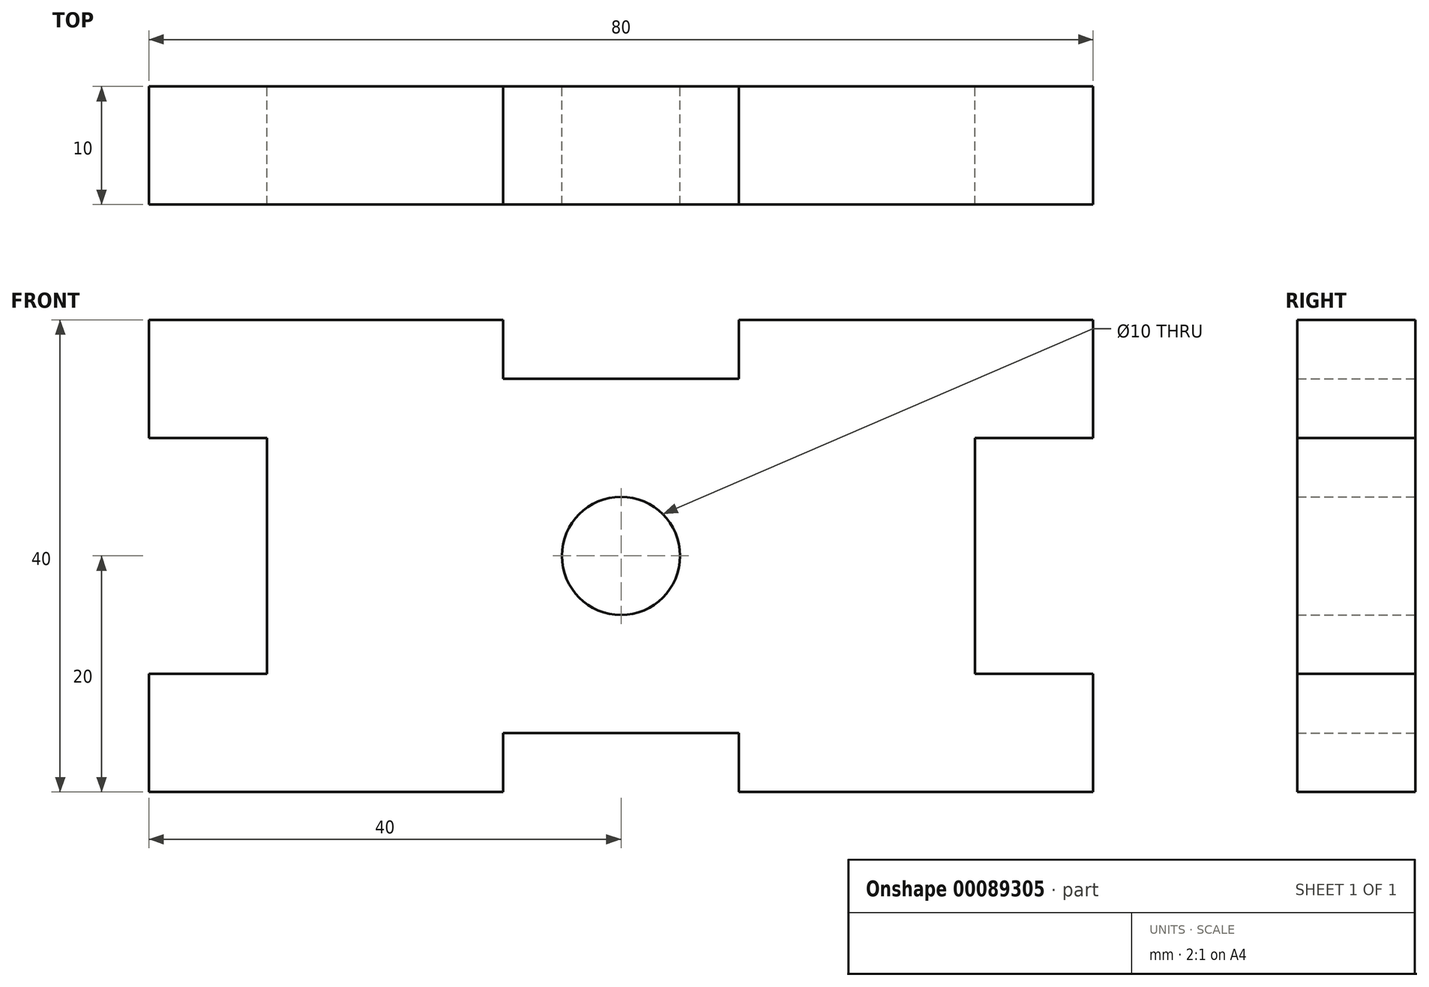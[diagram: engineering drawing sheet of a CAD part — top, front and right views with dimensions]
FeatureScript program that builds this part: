
annotation { "Feature Type Name" : "Feature", "Feature Type Description" : "" }
export const myFeature = defineFeature(function(context is Context, id is Id, definition is map)
    precondition{}
    {
        {
            var Q0;
            Q0=qCreatedBy(makeId("Front.planeOp"),FACE);
            var sketch = newSketch(context, id + "F0", { "sketchPlane" : qUnion([Q0])});
            skArc(sketch, "E0", {"start": v(5, 0) * mm, "mid": v(3.54, 3.54) * mm, "end": v(0, 5) * mm});
            skLineSegment(sketch, "E1", {"start": v(5, 0) * mm, "end": v(30, 0) * mm, "construction": true});
            skLineSegment(sketch, "E2", {"start": v(30, 0) * mm, "end": v(30, 10) * mm});
            skLineSegment(sketch, "E3", {"start": v(30, 10) * mm, "end": v(40, 10) * mm});
            skLineSegment(sketch, "E4", {"start": v(40, 10) * mm, "end": v(40, 20) * mm});
            skLineSegment(sketch, "E5", {"start": v(40, 20) * mm, "end": v(10, 20) * mm});
            skLineSegment(sketch, "E6", {"start": v(10, 20) * mm, "end": v(10, 15) * mm});
            skLineSegment(sketch, "E7", {"start": v(0, 5) * mm, "end": v(0, 15) * mm, "construction": true});
            skLineSegment(sketch, "E8", {"start": v(0, 15) * mm, "end": v(10, 15) * mm});
            skArc(sketch, "E9.MirrorCS", {"start": v(-5, 0) * mm, "mid": v(-3.54, 3.54) * mm, "end": v(0, 5) * mm});
            skLineSegment(sketch, "E10.MirrorCS", {"start": v(-40, 20) * mm, "end": v(-10, 20) * mm});
            skLineSegment(sketch, "E11.MirrorCS", {"start": v(-5, 0) * mm, "end": v(-30, 0) * mm, "construction": true});
            skLineSegment(sketch, "E12.MirrorCS", {"start": v(-30, 10) * mm, "end": v(-40, 10) * mm});
            skLineSegment(sketch, "E13.MirrorCS", {"start": v(-10, 20) * mm, "end": v(-10, 15) * mm});
            skLineSegment(sketch, "E14.MirrorCS", {"start": v(-40, 10) * mm, "end": v(-40, 20) * mm});
            skLineSegment(sketch, "E15.MirrorCS", {"start": v(0, 15) * mm, "end": v(-10, 15) * mm});
            skLineSegment(sketch, "E16.MirrorCS", {"start": v(-30, 0) * mm, "end": v(-30, 10) * mm});
            skLineSegment(sketch, "E17.MirrorCS", {"start": v(0, -15) * mm, "end": v(-10, -15) * mm});
            skArc(sketch, "E18.MirrorCS", {"start": v(5, 0) * mm, "mid": v(3.54, -3.54) * mm, "end": v(0, -5) * mm});
            skLineSegment(sketch, "E19.MirrorCS", {"start": v(-40, -10) * mm, "end": v(-40, -20) * mm});
            skLineSegment(sketch, "E20.MirrorCS", {"start": v(30, 0) * mm, "end": v(30, -10) * mm});
            skLineSegment(sketch, "E21.MirrorCS", {"start": v(30, -10) * mm, "end": v(40, -10) * mm});
            skLineSegment(sketch, "E22.MirrorCS", {"start": v(40, -10) * mm, "end": v(40, -20) * mm});
            skLineSegment(sketch, "E23.MirrorCS", {"start": v(40, -20) * mm, "end": v(10, -20) * mm});
            skLineSegment(sketch, "E24.MirrorCS", {"start": v(10, -20) * mm, "end": v(10, -15) * mm});
            skLineSegment(sketch, "E25.MirrorCS", {"start": v(0, -5) * mm, "end": v(0, -15) * mm, "construction": true});
            skLineSegment(sketch, "E26.MirrorCS", {"start": v(0, -15) * mm, "end": v(10, -15) * mm});
            skArc(sketch, "E27.MirrorCS", {"start": v(-5, 0) * mm, "mid": v(-3.54, -3.54) * mm, "end": v(0, -5) * mm});
            skLineSegment(sketch, "E28.MirrorCS", {"start": v(-30, -10) * mm, "end": v(-40, -10) * mm});
            skLineSegment(sketch, "E29.MirrorCS", {"start": v(-40, -20) * mm, "end": v(-10, -20) * mm});
            skLineSegment(sketch, "E30.MirrorCS", {"start": v(-10, -20) * mm, "end": v(-10, -15) * mm});
            skLineSegment(sketch, "E31.MirrorCS", {"start": v(-30, 0) * mm, "end": v(-30, -10) * mm});
            skSolve(sketch);
        }
        {
            var Q0;
            Q0=makeQuery(id+"F0.imprint","IMPRINT",FACE,{"disambiguationData":[TD([[makeQuery(id+"F0.imprint","IMPRINT",EDGE,{"derivedFrom":sQuery(id+"F0.wireOp",EDGE,"E0")}),-1.0]])]});
            extrude(context, id + "F1", {"entities" : qUnion([Q0]), "depth" : 10 * mm});
        }
    });
